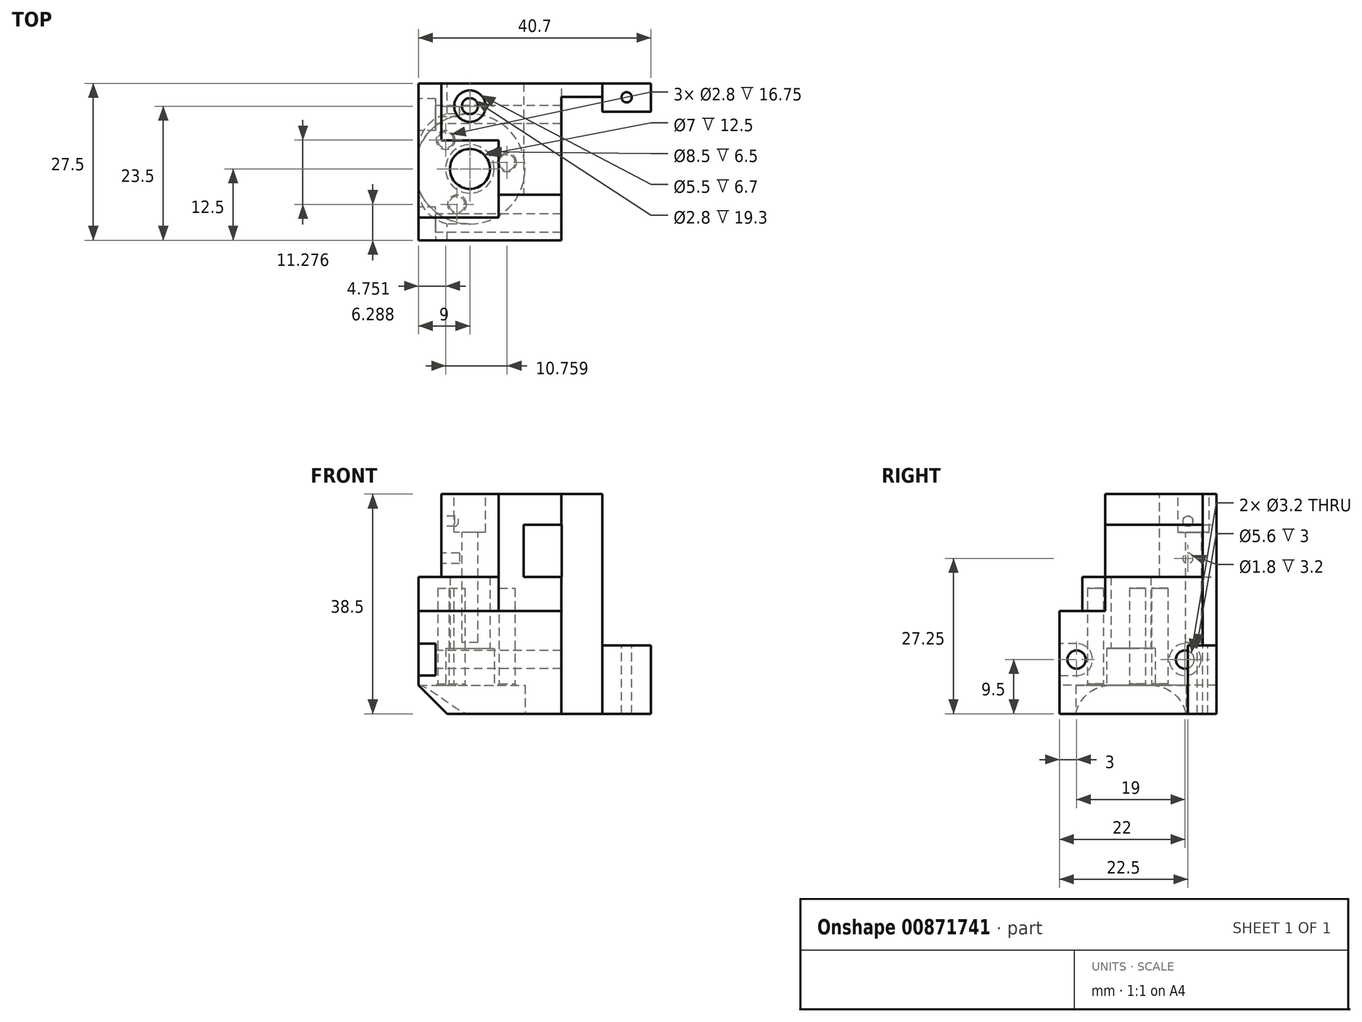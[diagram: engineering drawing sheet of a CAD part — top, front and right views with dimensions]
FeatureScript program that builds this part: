
annotation { "Feature Type Name" : "Feature", "Feature Type Description" : "" }
export const myFeature = defineFeature(function(context is Context, id is Id, definition is map)
    precondition{}
    {
        {
            var Q0;
            Q0=qCreatedBy(makeId("Right.planeOp"),FACE);
            var sketch = newSketch(context, id + "F0", { "sketchPlane" : qUnion([Q0])});
            skLineSegment(sketch, "E0", {"start": v(15, 0) * mm, "end": v(-12.5, 0) * mm});
            skLineSegment(sketch, "E1", {"start": v(-12.5, 0) * mm, "end": v(-12.5, 24) * mm});
            skLineSegment(sketch, "E2", {"start": v(-12.5, 24) * mm, "end": v(-10, 24) * mm});
            skLineSegment(sketch, "E3", {"start": v(-10, 24) * mm, "end": v(-10, 38.5) * mm});
            skLineSegment(sketch, "E4", {"start": v(-10, 38.5) * mm, "end": v(15, 38.5) * mm});
            skLineSegment(sketch, "E5", {"start": v(15, 38.5) * mm, "end": v(15, 0) * mm});
            skCircle(sketch, "E6", {"center": v(-9.5, 9.5) * mm, "radius": 1.6 * mm});
            skCircle(sketch, "E7", {"center": v(9.5, 9.5) * mm, "radius": 1.6 * mm});
            skLineSegment(sketch, "E8", {"start": v(9.5, 9.5) * mm, "end": v(-9.5, 9.5) * mm, "construction": true});
            skLineSegment(sketch, "E9", {"start": v(0, 0) * mm, "end": v(0, 9.5) * mm, "construction": true});
            skLineSegment(sketch, "E10", {"start": v(-9.5, 9.5) * mm, "end": v(-12.5, 9.5) * mm, "construction": true});
            skSolve(sketch);
        }
        {
            var Q0;
            Q0=makeQuery(id+"F0.imprint","IMPRINT",FACE,{"disambiguationData":[TD([[makeQuery(id+"F0.imprint","IMPRINT",EDGE,{"derivedFrom":sQuery(id+"F0.wireOp",EDGE,"E0")}),-1.0]])]});
            extrude(context, id + "F1", {"entities" : qUnion([Q0]), "depth" : 16 * mm, "offsetDistance" : 25 * mm, "hasSecondDirection" : true, "secondDirectionOppositeDirection" : true, "secondDirectionDepth" : 9 * mm});
        }
        {
            var Q0;
            Q0=makeQuery(id+"F1.opExtrude","CAP_FACE",FACE,{"disambiguationData":[OSD([sQuery(id+"F0.wireOp",EDGE,"E0"),sQuery(id+"F0.wireOp",EDGE,"E1"),sQuery(id+"F0.wireOp",EDGE,"E2"),sQuery(id+"F0.wireOp",EDGE,"E3"),sQuery(id+"F0.wireOp",EDGE,"E4"),sQuery(id+"F0.wireOp",EDGE,"E5"),sQuery(id+"F0.wireOp",EDGE,"E6"),sQuery(id+"F0.wireOp",EDGE,"E7")])],"isStart":false});
            var sketch = newSketch(context, id + "F2", { "sketchPlane" : qUnion([Q0])});
            skLineSegment(sketch, "E11.bottom", {"start": v(-8.03, 38.55) * mm, "end": v(-37.03, 38.55) * mm});
            skLineSegment(sketch, "E11.top", {"start": v(-8.03, 18.55) * mm, "end": v(-37.03, 18.55) * mm});
            skLineSegment(sketch, "E11.left", {"start": v(-8.03, 38.55) * mm, "end": v(-8.03, 18.55) * mm});
            skLineSegment(sketch, "E11.right", {"start": v(-37.03, 38.55) * mm, "end": v(-37.03, 18.55) * mm});
            skLineSegment(sketch, "E12.bottom", {"start": v(15, 33.1) * mm, "end": v(-50.4, 33.1) * mm});
            skLineSegment(sketch, "E12.top", {"start": v(15, 24) * mm, "end": v(-50.4, 24) * mm});
            skLineSegment(sketch, "E12.left", {"start": v(15, 33.1) * mm, "end": v(15, 24) * mm});
            skLineSegment(sketch, "E12.right", {"start": v(-50.4, 33.1) * mm, "end": v(-50.4, 24) * mm});
            skLineSegment(sketch, "E13", {"start": v(-8.03, 28.55) * mm, "end": v(15, 28.55) * mm, "construction": true});
            skSolve(sketch);
        }
        {
            var Q0;
            Q0=makeQuery(id+"F1.opExtrude","SWEPT_FACE",FACE,{"disambiguationData":[OSD([sQuery(id+"F0.wireOp",EDGE,"E0")])]});
            var sketch = newSketch(context, id + "F3", { "sketchPlane" : qUnion([Q0])});
            skCircle(sketch, "E14", {"center": v(0, 0) * mm, "radius": 3.5 * mm});
            skCircle(sketch, "E15", {"center": v(-2.26, 6.21) * mm, "radius": 1.4 * mm});
            skCircle(sketch, "E16", {"center": v(-4.25, -5.06) * mm, "radius": 1.4 * mm});
            skCircle(sketch, "E17", {"center": v(6.51, -1.15) * mm, "radius": 1.4 * mm});
            skLineSegment(sketch, "E18", {"start": v(0, 0) * mm, "end": v(6.51, -1.15) * mm, "construction": true});
            skLineSegment(sketch, "E19", {"start": v(-2.26, 6.21) * mm, "end": v(6.51, -1.15) * mm, "construction": true});
            skLineSegment(sketch, "E20", {"start": v(-2.26, 6.21) * mm, "end": v(-4.25, -5.06) * mm, "construction": true});
            skLineSegment(sketch, "E21", {"start": v(6.51, -1.15) * mm, "end": v(-4.25, -5.06) * mm, "construction": true});
            skLineSegment(sketch, "E22", {"start": v(0, 0) * mm, "end": v(-4.25, -5.06) * mm, "construction": true});
            skLineSegment(sketch, "E23", {"start": v(0, 0) * mm, "end": v(-2.26, 6.21) * mm, "construction": true});
            skLineSegment(sketch, "E24", {"start": v(0, 0) * mm, "end": v(-17.05, 0) * mm, "construction": true});
            skSolve(sketch);
        }
        {
            var Q0;
            Q0=qSketchRegion(id+"F3",true);
            extrude(context, id + "F4", {"entities" : qUnion([Q0]), "operationType" : NewBodyOperationType.REMOVE, "oppositeDirection" : true, "depth" : 22 * mm, "offsetDistance" : 25 * mm});
        }
        {
            var Q0;
            Q0=makeQuery(id+"F4.boolean.opBoolean","COPY",FACE,{"derivedFrom":makeQuery(id+"F4.opExtrude","CAP_FACE",FACE,{"disambiguationData":[OSD([sQuery(id+"F3.wireOp",EDGE,"E14")])],"isStart":false})});
            extrude(context, id + "F5", {"entities" : qUnion([Q0]), "operationType" : NewBodyOperationType.REMOVE, "endBound" : BoundingType.THROUGH_ALL, "oppositeDirection" : true, "depth" : 25 * mm, "offsetDistance" : 25 * mm});
        }
        {
            var Q0;
            Q0=makeQuery(id+"F1.opExtrude","SWEPT_FACE",FACE,{"disambiguationData":[OSD([sQuery(id+"F0.wireOp",EDGE,"E2")])]});
            cPlane(context, id + "F6", {"entities" : qUnion([Q0]), "cplaneType" : CPlaneType.OFFSET, "offset" : 10 * mm, "oppositeDirection" : true, "width" : 150 * mm, "height" : 150 * mm});
        }
        {
            var Q0;
            Q0=makeQuery(id+"F1.opExtrude","SWEPT_FACE",FACE,{"disambiguationData":[OSD([sQuery(id+"F0.wireOp",EDGE,"E0")])]});
            var sketch = newSketch(context, id + "F7", { "sketchPlane" : qUnion([Q0])});
            skCircle(sketch, "E25", {"center": v(-2.26, 6.21) * mm, "radius": 1.65 * mm});
            skCircle(sketch, "E26", {"center": v(-4.25, -5.06) * mm, "radius": 1.65 * mm});
            skCircle(sketch, "E27", {"center": v(6.51, -1.15) * mm, "radius": 1.65 * mm});
            skSolve(sketch);
        }
        {
            var Q0;
            Q0=makeQuery(id+"F1.opExtrude","SWEPT_FACE",FACE,{"disambiguationData":[OSD([sQuery(id+"F0.wireOp",EDGE,"E0")])]});
            var sketch = newSketch(context, id + "F8", { "sketchPlane" : qUnion([Q0])});
            skCircle(sketch, "E28", {"center": v(0, 0) * mm, "radius": 9.65 * mm});
            skPoint(sketch, "E29", {"position": v(0, 9.65) * mm});
            skSolve(sketch);
        }
        {
            var Q0;
            Q0=qSketchRegion(id+"F8",true);
            extrude(context, id + "F9", {"entities" : qUnion([Q0]), "operationType" : NewBodyOperationType.REMOVE, "oppositeDirection" : true, "depth" : 5 * mm, "offsetDistance" : 25 * mm});
        }
        {
            var Q0;
            Q0=makeQuery(id+"F9.boolean.opBoolean","COPY",FACE,{"derivedFrom":makeQuery(id+"F9.opExtrude","CAP_FACE",FACE,{"disambiguationData":[OSD([sQuery(id+"F8.wireOp",EDGE,"E28")])],"isStart":false})});
            var sketch = newSketch(context, id + "F10", { "sketchPlane" : qUnion([Q0])});
            skCircle(sketch, "E30", {"center": v(0, 0) * mm, "radius": 4.25 * mm});
            skSolve(sketch);
        }
        {
            var Q0;
            Q0=qSketchRegion(id+"F10",true);
            extrude(context, id + "F11", {"entities" : qUnion([Q0]), "operationType" : NewBodyOperationType.REMOVE, "oppositeDirection" : true, "depth" : 6.5 * mm, "offsetDistance" : 25 * mm});
        }
        {
            var Q0;
            Q0=makeQuery(id+"F1.opExtrude","CAP_FACE",FACE,{"disambiguationData":[OSD([sQuery(id+"F0.wireOp",EDGE,"E0"),sQuery(id+"F0.wireOp",EDGE,"E1"),sQuery(id+"F0.wireOp",EDGE,"E2"),sQuery(id+"F0.wireOp",EDGE,"E3"),sQuery(id+"F0.wireOp",EDGE,"E4"),sQuery(id+"F0.wireOp",EDGE,"E5"),sQuery(id+"F0.wireOp",EDGE,"E6"),sQuery(id+"F0.wireOp",EDGE,"E7")])],"isStart":false});
            var sketch = newSketch(context, id + "F12", { "sketchPlane" : qUnion([Q0])});
            skLineSegment(sketch, "E31.bottom", {"start": v(15, 24) * mm, "end": v(-10, 24) * mm});
            skLineSegment(sketch, "E31.top", {"start": v(15, 33.1) * mm, "end": v(-10, 33.1) * mm});
            skLineSegment(sketch, "E31.left", {"start": v(-10, 24) * mm, "end": v(-10, 33.1) * mm});
            skLineSegment(sketch, "E31.right", {"start": v(15, 24) * mm, "end": v(15, 33.1) * mm});
            skLineSegment(sketch, "E32", {"start": v(9.5, 9.5) * mm, "end": v(9.5, 24) * mm, "construction": true});
            skSolve(sketch);
        }
        {
            var Q0;
            Q0=qSketchRegion(id+"F12",true);
            extrude(context, id + "F13", {"entities" : qUnion([Q0]), "operationType" : NewBodyOperationType.REMOVE, "oppositeDirection" : true, "depth" : 6.6 * mm, "offsetDistance" : 25 * mm});
        }
        {
            var Q0;
            Q0=makeQuery(id+"F1.opExtrude","CAP_FACE",FACE,{"disambiguationData":[OSD([sQuery(id+"F0.wireOp",EDGE,"E0"),sQuery(id+"F0.wireOp",EDGE,"E1"),sQuery(id+"F0.wireOp",EDGE,"E2"),sQuery(id+"F0.wireOp",EDGE,"E3"),sQuery(id+"F0.wireOp",EDGE,"E4"),sQuery(id+"F0.wireOp",EDGE,"E5"),sQuery(id+"F0.wireOp",EDGE,"E6"),sQuery(id+"F0.wireOp",EDGE,"E7")])],"isStart":true});
            var sketch = newSketch(context, id + "F14", { "sketchPlane" : qUnion([Q0])});
            skCircle(sketch, "E33", {"center": v(-9.5, 9.5) * mm, "radius": 2.8 * mm});
            skCircle(sketch, "E34", {"center": v(9.5, 9.5) * mm, "radius": 2.8 * mm});
            skLineSegment(sketch, "E35", {"start": v(9.5, 12.3) * mm, "end": v(12.5, 12.3) * mm});
            skLineSegment(sketch, "E36", {"start": v(12.5, 12.3) * mm, "end": v(12.5, 6.7) * mm});
            skLineSegment(sketch, "E37", {"start": v(12.5, 6.7) * mm, "end": v(9.5, 6.7) * mm});
            skSolve(sketch);
        }
        {
            var Q0;
            Q0=qSketchRegion(id+"F14",true);
            extrude(context, id + "F15", {"entities" : qUnion([Q0]), "operationType" : NewBodyOperationType.REMOVE, "oppositeDirection" : true, "depth" : 3 * mm, "offsetDistance" : 25 * mm});
        }
        {
            var Q0;
            Q0=makeQuery(id+"F1.opExtrude","CAP_FACE",FACE,{"disambiguationData":[OSD([sQuery(id+"F0.wireOp",EDGE,"E0"),sQuery(id+"F0.wireOp",EDGE,"E1"),sQuery(id+"F0.wireOp",EDGE,"E2"),sQuery(id+"F0.wireOp",EDGE,"E3"),sQuery(id+"F0.wireOp",EDGE,"E4"),sQuery(id+"F0.wireOp",EDGE,"E5"),sQuery(id+"F0.wireOp",EDGE,"E6"),sQuery(id+"F0.wireOp",EDGE,"E7")])],"isStart":false});
            var sketch = newSketch(context, id + "F16", { "sketchPlane" : qUnion([Q0])});
            skLineSegment(sketch, "E38.bottom", {"start": v(-4.5, 24) * mm, "end": v(-12.5, 24) * mm});
            skLineSegment(sketch, "E38.top", {"start": v(-4.5, 18) * mm, "end": v(-12.5, 18) * mm});
            skLineSegment(sketch, "E38.left", {"start": v(-12.5, 24) * mm, "end": v(-12.5, 18) * mm});
            skLineSegment(sketch, "E38.right", {"start": v(-4.5, 24) * mm, "end": v(-4.5, 18) * mm});
            skLineSegment(sketch, "E39", {"start": v(-4.5, 24) * mm, "end": v(-4.5, 33.1) * mm});
            skLineSegment(sketch, "E40", {"start": v(-4.5, 33.1) * mm, "end": v(-12.5, 33.1) * mm});
            skLineSegment(sketch, "E41", {"start": v(-12.5, 33.1) * mm, "end": v(-12.5, 24) * mm});
            skSolve(sketch);
        }
        {
            var Q0;
            Q0=qSketchRegion(id+"F16",true);
            extrude(context, id + "F17", {"entities" : qUnion([Q0]), "operationType" : NewBodyOperationType.REMOVE, "oppositeDirection" : true, "depth" : 11 * mm, "offsetDistance" : 25 * mm});
        }
        {
            var Q0;
            Q0=makeQuery(id+"F1.opExtrude","SWEPT_FACE",FACE,{"disambiguationData":[OSD([sQuery(id+"F0.wireOp",EDGE,"E4")])]});
            var sketch = newSketch(context, id + "F18", { "sketchPlane" : qUnion([Q0])});
            skLineSegment(sketch, "E42", {"start": v(16, 11) * mm, "end": v(-9, 11) * mm, "construction": true});
            skSolve(sketch);
        }
        {
            var Q0;
            Q0=sQuery(id+"F18.wireOp",EDGE,"E42");
            cPoint(context, id + "F19", {"entities" : qUnion([Q0]), "parameter" : 0.5});
        }
        {
            var Q0;
            Q0=qCreatedBy(makeId("Front.planeOp"),FACE);
            var Q1;
            Q1=qCreatedBy(id+"F19",VERTEX);
            cPlane(context, id + "F20", {"entities" : qUnion([Q0, Q1]), "cplaneType" : CPlaneType.PLANE_POINT, "offset" : 25 * mm, "width" : 150 * mm, "height" : 150 * mm});
        }
        {
            var Q0;
            Q0=qCreatedBy(id+"F20.planeOp",FACE);
            var sketch = newSketch(context, id + "F21", { "sketchPlane" : qUnion([Q0])});
            skLineSegment(sketch, "E43", {"start": v(0, 38.5) * mm, "end": v(-2.75, 38.5) * mm});
            skLineSegment(sketch, "E44", {"start": v(-2.75, 38.5) * mm, "end": v(-2.75, 31.8) * mm});
            skLineSegment(sketch, "E45", {"start": v(-2.75, 31.8) * mm, "end": v(-1.4, 31.8) * mm});
            skLineSegment(sketch, "E46", {"start": v(-1.4, 31.8) * mm, "end": v(-1.4, 12.5) * mm});
            skLineSegment(sketch, "E47", {"start": v(0, 12.5) * mm, "end": v(0, 38.5) * mm});
            skLineSegment(sketch, "E48", {"start": v(-1.4, 12.5) * mm, "end": v(0, 12.5) * mm});
            skSolve(sketch);
        }
        {
            var Q0;
            Q0=qSketchRegion(id+"F21",true);
            var Q1;
            Q1=sQuery(id+"F21.wireOp",EDGE,"E47");
            revolve(context, id + "F22", {"operationType" : NewBodyOperationType.REMOVE, "surfaceOperationType" : NewSurfaceOperationType.NEW, "entities" : qUnion([Q0]), "axis" : qUnion([Q1]), "revolveType" : RevolveType.FULL, "oppositeDirection" : true});
        }
        {
            var Q0;
            {var subQ0=sQuery(id+"F0.wireOp",EDGE,"E3");var subQ1=sQuery(id+"F0.wireOp",EDGE,"E4");var subQ2=sQuery(id+"F0.wireOp",EDGE,"E5");Q0=makeQuery(id+"F13.boolean.opBoolean","SPLIT",FACE,{"disambiguationData":[TD([makeQuery(id+"F1.opExtrude","SWEPT_FACE",FACE,{"disambiguationData":[OSD([subQ0])]})])],"derivedFrom":makeQuery(id+"F1.opExtrude","CAP_FACE",FACE,{"disambiguationData":[OSD([sQuery(id+"F0.wireOp",EDGE,"E0"),sQuery(id+"F0.wireOp",EDGE,"E1"),sQuery(id+"F0.wireOp",EDGE,"E2"),subQ0,subQ1,subQ2,sQuery(id+"F0.wireOp",EDGE,"E6"),sQuery(id+"F0.wireOp",EDGE,"E7")])],"isStart":false})});}
            var sketch = newSketch(context, id + "F23", { "sketchPlane" : qUnion([Q0])});
            skLineSegment(sketch, "E49", {"start": v(-12.5, 24) * mm, "end": v(-4.5, 24) * mm});
            skLineSegment(sketch, "E50", {"start": v(-4.5, 24) * mm, "end": v(-4.5, 38.5) * mm});
            skLineSegment(sketch, "E51", {"start": v(-4.5, 38.5) * mm, "end": v(-12.5, 38.5) * mm});
            skLineSegment(sketch, "E52", {"start": v(-12.5, 38.5) * mm, "end": v(-12.5, 24) * mm});
            skSolve(sketch);
        }
        {
            var Q0;
            Q0 = qSketchRegion(id + "F23", true);
            extrude(context, id + "F24", {"entities" : qUnion([Q0]), "operationType" : NewBodyOperationType.REMOVE, "endBound" : BoundingType.THROUGH_ALL, "oppositeDirection" : true, "depth" : 25 * mm, "offsetDistance" : 25 * mm});
        }
        {
            var Q0;
            Q0=makeQuery(id+"F1.opExtrude","SWEPT_FACE",FACE,{"disambiguationData":[OSD([sQuery(id+"F0.wireOp",EDGE,"E4")])]});
            var sketch = newSketch(context, id + "F25", { "sketchPlane" : qUnion([Q0])});
            skLineSegment(sketch, "E53.bottom", {"start": v(-9, -4.5) * mm, "end": v(5, -4.5) * mm});
            skLineSegment(sketch, "E53.top", {"start": v(-9, 5) * mm, "end": v(5, 5) * mm});
            skLineSegment(sketch, "E53.left", {"start": v(-9, -4.5) * mm, "end": v(-9, 5) * mm});
            skLineSegment(sketch, "E53.right", {"start": v(5, -4.5) * mm, "end": v(5, 5) * mm});
            skSolve(sketch);
        }
        {
            var Q0;
            Q0 = qSketchRegion(id + "F25", true);
            var Q1;
            {var subQ1=sQuery(id+"F0.wireOp",EDGE,"E2");var subQ2=sQuery(id+"F0.wireOp",EDGE,"E1");Q1=makeQuery(id+"F24.boolean.opBoolean","MERGE",FACE,{"derivedFrom":[makeQuery(id+"F17.boolean.opBoolean","SPLIT",FACE,{"disambiguationData":[TD([makeQuery(id+"F1.opExtrude","SWEPT_FACE",FACE,{"disambiguationData":[OSD([subQ2])]})])],"derivedFrom":makeQuery(id+"F13.boolean.opBoolean","MERGE",FACE,{"derivedFrom":[makeQuery(id+"F1.opExtrude","SWEPT_FACE",FACE,{"disambiguationData":[OSD([subQ1])]})],"fromTools":[makeQuery(id+"F13.opExtrude","SWEPT_FACE",FACE,{"disambiguationData":[OSD([sQuery(id+"F12.wireOp",EDGE,"E31.bottom")])]})]})})],"fromTools":[makeQuery(id+"F24.opExtrude","SWEPT_FACE",FACE,{"disambiguationData":[OSD([sQuery(id+"F23.wireOp",EDGE,"E49")])]})]});}
            extrude(context, id + "F26", {"entities" : qUnion([Q0]), "operationType" : NewBodyOperationType.REMOVE, "endBound" : BoundingType.UP_TO_SURFACE, "oppositeDirection" : true, "depth" : 25 * mm, "endBoundEntityFace" : qUnion([Q1]), "offsetDistance" : 25 * mm});
        }
        {
            var Q0;
            Q0=makeQuery(id+"F1.opExtrude","CAP_FACE",FACE,{"disambiguationData":[OSD([sQuery(id+"F0.wireOp",EDGE,"E0"),sQuery(id+"F0.wireOp",EDGE,"E1"),sQuery(id+"F0.wireOp",EDGE,"E2"),sQuery(id+"F0.wireOp",EDGE,"E3"),sQuery(id+"F0.wireOp",EDGE,"E4"),sQuery(id+"F0.wireOp",EDGE,"E5"),sQuery(id+"F0.wireOp",EDGE,"E6"),sQuery(id+"F0.wireOp",EDGE,"E7")])],"isStart":true});
            var sketch = newSketch(context, id + "F27", { "sketchPlane" : qUnion([Q0])});
            skLineSegment(sketch, "E54", {"start": v(3.48, 5) * mm, "end": v(9.65, 0) * mm, "construction": true});
            skLineSegment(sketch, "E55", {"start": v(9.65, 0) * mm, "end": v(-9.65, 0) * mm});
            skLineSegment(sketch, "E56", {"start": v(-9.65, 0) * mm, "end": v(-3.48, 5) * mm, "construction": true});
            skLineSegment(sketch, "E57", {"start": v(-3.48, 5) * mm, "end": v(3.48, 5) * mm});
            skPoint(sketch, "E58", {"position": v(8, 0) * mm});
            skArc(sketch, "E59", {"start": v(9.65, 0) * mm, "mid": v(7.45, 3.6) * mm, "end": v(3.48, 5) * mm});
            skArc(sketch, "E60", {"start": v(-3.48, 5) * mm, "mid": v(-7.45, 3.6) * mm, "end": v(-9.65, 0) * mm});
            skSolve(sketch);
        }
        {
            var Q0;
            Q0 = qSketchRegion(id + "F27", true);
            extrude(context, id + "F28", {"entities" : qUnion([Q0]), "operationType" : NewBodyOperationType.REMOVE, "endBound" : BoundingType.UP_TO_NEXT, "oppositeDirection" : true, "depth" : 25 * mm, "offsetDistance" : 25 * mm});
        }
        {
            var Q0;
            {var subQ1=sQuery(id+"F0.wireOp",EDGE,"E2");var subQ2=sQuery(id+"F0.wireOp",EDGE,"E1");Q0=makeQuery(id+"F26.boolean.opBoolean","MERGE",FACE,{"derivedFrom":[makeQuery(id+"F24.boolean.opBoolean","MERGE",FACE,{"derivedFrom":[makeQuery(id+"F17.boolean.opBoolean","SPLIT",FACE,{"disambiguationData":[TD([makeQuery(id+"F1.opExtrude","SWEPT_FACE",FACE,{"disambiguationData":[OSD([subQ2])]})])],"derivedFrom":makeQuery(id+"F13.boolean.opBoolean","MERGE",FACE,{"derivedFrom":[makeQuery(id+"F1.opExtrude","SWEPT_FACE",FACE,{"disambiguationData":[OSD([subQ1])]})],"fromTools":[makeQuery(id+"F13.opExtrude","SWEPT_FACE",FACE,{"disambiguationData":[OSD([sQuery(id+"F12.wireOp",EDGE,"E31.bottom")])]})]})})],"fromTools":[makeQuery(id+"F24.opExtrude","SWEPT_FACE",FACE,{"disambiguationData":[OSD([sQuery(id+"F23.wireOp",EDGE,"E49")])]})]})],"fromTools":[makeQuery(id+"F26.opExtrude","CAP_FACE",FACE,{"disambiguationData":[OSD([sQuery(id+"F25.wireOp",EDGE,"E53.bottom"),sQuery(id+"F25.wireOp",EDGE,"E53.top"),sQuery(id+"F25.wireOp",EDGE,"E53.left"),sQuery(id+"F25.wireOp",EDGE,"E53.right")])],"isStart":false})]});}
            var sketch = newSketch(context, id + "F29", { "sketchPlane" : qUnion([Q0])});
            skLineSegment(sketch, "E61.bottom", {"start": v(-9, -12.5) * mm, "end": v(5, -12.5) * mm});
            skLineSegment(sketch, "E61.top", {"start": v(-9, -8.5) * mm, "end": v(5, -8.5) * mm});
            skLineSegment(sketch, "E61.left", {"start": v(-9, -12.5) * mm, "end": v(-9, -8.5) * mm});
            skLineSegment(sketch, "E61.right", {"start": v(5, -12.5) * mm, "end": v(5, -8.5) * mm});
            skSolve(sketch);
        }
        {
            var Q0;
            Q0 = qSketchRegion(id + "F29", true);
            var Q1;
            Q1=makeQuery(id+"F17.boolean.opBoolean","COPY",FACE,{"derivedFrom":makeQuery(id+"F17.opExtrude","SWEPT_FACE",FACE,{"disambiguationData":[OSD([sQuery(id+"F16.wireOp",EDGE,"E38.top")])]})});
            extrude(context, id + "F30", {"entities" : qUnion([Q0]), "operationType" : NewBodyOperationType.REMOVE, "endBound" : BoundingType.UP_TO_SURFACE, "oppositeDirection" : true, "depth" : 25 * mm, "endBoundEntityFace" : qUnion([Q1]), "offsetDistance" : 25 * mm});
        }
        {
            var Q0;
            Q0=makeQuery(id+"F1.opExtrude","SWEPT_FACE",FACE,{"disambiguationData":[OSD([sQuery(id+"F0.wireOp",EDGE,"E5")])]});
            var sketch = newSketch(context, id + "F31", { "sketchPlane" : qUnion([Q0])});
            skLineSegment(sketch, "E62.bottom", {"start": v(-16, 0) * mm, "end": v(-23.2, 0) * mm});
            skLineSegment(sketch, "E62.top", {"start": v(-16, 38.5) * mm, "end": v(-23.2, 38.5) * mm});
            skLineSegment(sketch, "E62.left", {"start": v(-16, 0) * mm, "end": v(-16, 24) * mm});
            skLineSegment(sketch, "E62.right", {"start": v(-23.2, 0) * mm, "end": v(-23.2, 38.5) * mm});
            skLineSegment(sketch, "E63", {"start": v(-16, 24) * mm, "end": v(-16.1, 24) * mm});
            skLineSegment(sketch, "E64", {"start": v(-16.1, 24) * mm, "end": v(-16.1, 33.1) * mm});
            skLineSegment(sketch, "E65", {"start": v(-16.1, 33.1) * mm, "end": v(-16, 33.1) * mm});
            skLineSegment(sketch, "E66.trimOffspring", {"start": v(-16, 33.1) * mm, "end": v(-16, 38.5) * mm});
            skSolve(sketch);
        }
        {
            var Q0;
            Q0 = qSketchRegion(id + "F31", true);
            extrude(context, id + "F32", {"entities" : qUnion([Q0]), "operationType" : NewBodyOperationType.ADD, "oppositeDirection" : true, "depth" : 2.4 * mm, "offsetDistance" : 25 * mm});
        }
        {
            var Q0;
            Q0=makeQuery(id+"F1.opExtrude","CAP_FACE",FACE,{"disambiguationData":[OSD([sQuery(id+"F0.wireOp",EDGE,"E0"),sQuery(id+"F0.wireOp",EDGE,"E1"),sQuery(id+"F0.wireOp",EDGE,"E2"),sQuery(id+"F0.wireOp",EDGE,"E3"),sQuery(id+"F0.wireOp",EDGE,"E4"),sQuery(id+"F0.wireOp",EDGE,"E5"),sQuery(id+"F0.wireOp",EDGE,"E6"),sQuery(id+"F0.wireOp",EDGE,"E7")])],"isStart":true});
            var sketch = newSketch(context, id + "F33", { "sketchPlane" : qUnion([Q0])});
            skLineSegment(sketch, "E67.bottom", {"start": v(-5, 38.5) * mm, "end": v(-15, 38.5) * mm});
            skLineSegment(sketch, "E67.top", {"start": v(-5, 24) * mm, "end": v(-15, 24) * mm});
            skLineSegment(sketch, "E67.left", {"start": v(-5, 38.5) * mm, "end": v(-5, 24) * mm});
            skLineSegment(sketch, "E67.right", {"start": v(-15, 38.5) * mm, "end": v(-15, 24) * mm});
            skSolve(sketch);
        }
        {
            var Q0;
            Q0 = qSketchRegion(id + "F33", true);
            extrude(context, id + "F34", {"entities" : qUnion([Q0]), "operationType" : NewBodyOperationType.REMOVE, "oppositeDirection" : true, "depth" : 4 * mm, "offsetDistance" : 25 * mm});
        }
        {
            var Q0;
            Q0=makeQuery(id+"F34.boolean.opBoolean","COPY",FACE,{"derivedFrom":makeQuery(id+"F34.opExtrude","CAP_FACE",FACE,{"disambiguationData":[OSD([sQuery(id+"F33.wireOp",EDGE,"E67.bottom"),sQuery(id+"F33.wireOp",EDGE,"E67.top"),sQuery(id+"F33.wireOp",EDGE,"E67.left"),sQuery(id+"F33.wireOp",EDGE,"E67.right")])],"isStart":false})});
            var sketch = newSketch(context, id + "F35", { "sketchPlane" : qUnion([Q0])});
            skCircle(sketch, "E68", {"center": v(-10, 33.75) * mm, "radius": 0.9 * mm});
            skCircle(sketch, "E69", {"center": v(-10, 27.25) * mm, "radius": 0.9 * mm});
            skLineSegment(sketch, "E70", {"start": v(-10, 27.25) * mm, "end": v(-10, 33.75) * mm, "construction": true});
            skPoint(sketch, "E71", {"position": v(-10, 30.5) * mm});
            skSolve(sketch);
        }
        {
            var Q0;
            Q0 = qSketchRegion(id + "F35", true);
            extrude(context, id + "F36", {"entities" : qUnion([Q0]), "operationType" : NewBodyOperationType.REMOVE, "oppositeDirection" : true, "depth" : 3.2 * mm, "offsetDistance" : 25 * mm});
        }
        {
            var Q0;
            Q0=makeQuery(id+"F32.boolean.opBoolean","MERGE",FACE,{"derivedFrom":[makeQuery(id+"F1.opExtrude","SWEPT_FACE",FACE,{"disambiguationData":[OSD([sQuery(id+"F0.wireOp",EDGE,"E5")])]}),makeQuery(id+"F32.opExtrude","CAP_FACE",FACE,{"disambiguationData":[OSD([sQuery(id+"F31.wireOp",EDGE,"E62.bottom"),sQuery(id+"F31.wireOp",EDGE,"E62.top"),sQuery(id+"F31.wireOp",EDGE,"E62.left"),sQuery(id+"F31.wireOp",EDGE,"E62.right"),sQuery(id+"F31.wireOp",EDGE,"E63"),sQuery(id+"F31.wireOp",EDGE,"E64"),sQuery(id+"F31.wireOp",EDGE,"E65"),sQuery(id+"F31.wireOp",EDGE,"E66.trimOffspring")])],"isStart":true})]});
            var sketch = newSketch(context, id + "F37", { "sketchPlane" : qUnion([Q0])});
            skLineSegment(sketch, "E72.bottom", {"start": v(-23.2, 0) * mm, "end": v(-31.7, 0) * mm});
            skLineSegment(sketch, "E72.top", {"start": v(-23.2, 12) * mm, "end": v(-31.7, 12) * mm});
            skLineSegment(sketch, "E72.left", {"start": v(-23.2, 0) * mm, "end": v(-23.2, 12) * mm});
            skLineSegment(sketch, "E72.right", {"start": v(-31.7, 0) * mm, "end": v(-31.7, 12) * mm});
            skSolve(sketch);
        }
        {
            var Q0;
            Q0 = qSketchRegion(id + "F37", true);
            extrude(context, id + "F38", {"entities" : qUnion([Q0]), "operationType" : NewBodyOperationType.ADD, "oppositeDirection" : true, "depth" : 5 * mm, "offsetDistance" : 25 * mm});
        }
        {
            var Q0;
            Q0=makeQuery(id+"F38.opExtrude","SWEPT_FACE",FACE,{"disambiguationData":[OSD([sQuery(id+"F37.wireOp",EDGE,"E72.top")])]});
            var sketch = newSketch(context, id + "F39", { "sketchPlane" : qUnion([Q0])});
            skCircle(sketch, "E73", {"center": v(27.45, 12.55) * mm, "radius": 0.9 * mm});
            skLineSegment(sketch, "E74", {"start": v(31.7, 12.5) * mm, "end": v(23.2, 12.6) * mm, "construction": true});
            skSolve(sketch);
        }
        {
            var Q0;
            Q0=makeQuery(id+"F39.imprint","IMPRINT",FACE,{"disambiguationData":[TD([[makeQuery(id+"F39.imprint","IMPRINT",EDGE,{"derivedFrom":sQuery(id+"F39.wireOp",EDGE,"E73")}),1.0]])]});
            var Q1;
            Q1=sQuery(id+"F39.wireOp",EDGE,"E74");
            extrude(context, id + "F40", {"entities" : qUnion([Q0]), "operationType" : NewBodyOperationType.REMOVE, "surfaceEntities" : qUnion([Q1]), "endBound" : BoundingType.UP_TO_NEXT, "oppositeDirection" : true, "depth" : 25 * mm, "offsetDistance" : 25 * mm});
        }
        {
            var Q0;
            Q0=makeQuery(id+"F9.boolean.opBoolean","INTERSECT",EDGE,{"derivedFrom":[makeQuery(id+"F4.boolean.opBoolean","COPY",FACE,{"derivedFrom":makeQuery(id+"F4.opExtrude","SWEPT_FACE",FACE,{"disambiguationData":[OSD([sQuery(id+"F3.wireOp",EDGE,"E15")])]})}),makeQuery(id+"F9.opExtrude","CAP_FACE",FACE,{"disambiguationData":[OSD([sQuery(id+"F8.wireOp",EDGE,"E28")])],"isStart":false})]});
            var Q1;
            Q1=makeQuery(id+"F9.boolean.opBoolean","INTERSECT",EDGE,{"derivedFrom":[makeQuery(id+"F4.boolean.opBoolean","COPY",FACE,{"derivedFrom":makeQuery(id+"F4.opExtrude","SWEPT_FACE",FACE,{"disambiguationData":[OSD([sQuery(id+"F3.wireOp",EDGE,"E17")])]})}),makeQuery(id+"F9.opExtrude","CAP_FACE",FACE,{"disambiguationData":[OSD([sQuery(id+"F8.wireOp",EDGE,"E28")])],"isStart":false})]});
            var Q2;
            Q2=makeQuery(id+"F9.boolean.opBoolean","INTERSECT",EDGE,{"derivedFrom":[makeQuery(id+"F4.boolean.opBoolean","COPY",FACE,{"derivedFrom":makeQuery(id+"F4.opExtrude","SWEPT_FACE",FACE,{"disambiguationData":[OSD([sQuery(id+"F3.wireOp",EDGE,"E16")])]})}),makeQuery(id+"F9.opExtrude","CAP_FACE",FACE,{"disambiguationData":[OSD([sQuery(id+"F8.wireOp",EDGE,"E28")])],"isStart":false})]});
            chamfer(context, id + "F41", {"entities" : qUnion([Q0, Q1, Q2]), "width" : 0.25 * mm, "tangentPropagation" : true});
        }
        {
            var Q0;
            {var subQ0=sQuery(id+"F0.wireOp",EDGE,"E0");var subQ1=sQuery(id+"F0.wireOp",EDGE,"E5");Q0=makeQuery(id+"F9.boolean.opBoolean","SPLIT",EDGE,{"disambiguationData":[TD([makeQuery(id+"F1.opExtrude","SWEPT_FACE",FACE,{"disambiguationData":[OSD([subQ1])]})])],"derivedFrom":makeQuery(id+"F1.opExtrude","CAP_EDGE",EDGE,{"disambiguationData":[OSD([subQ0])],"isStart":true})});}
            var Q1;
            {var subQ0=sQuery(id+"F0.wireOp",EDGE,"E0");var subQ1=sQuery(id+"F0.wireOp",EDGE,"E1");Q1=makeQuery(id+"F9.boolean.opBoolean","SPLIT",EDGE,{"disambiguationData":[TD([makeQuery(id+"F1.opExtrude","SWEPT_FACE",FACE,{"disambiguationData":[OSD([subQ1])]})])],"derivedFrom":makeQuery(id+"F1.opExtrude","CAP_EDGE",EDGE,{"disambiguationData":[OSD([subQ0])],"isStart":true})});}
            chamfer(context, id + "F42", {"entities" : qUnion([Q0, Q1]), "width" : 5 * mm, "tangentPropagation" : true});
        }
    });
